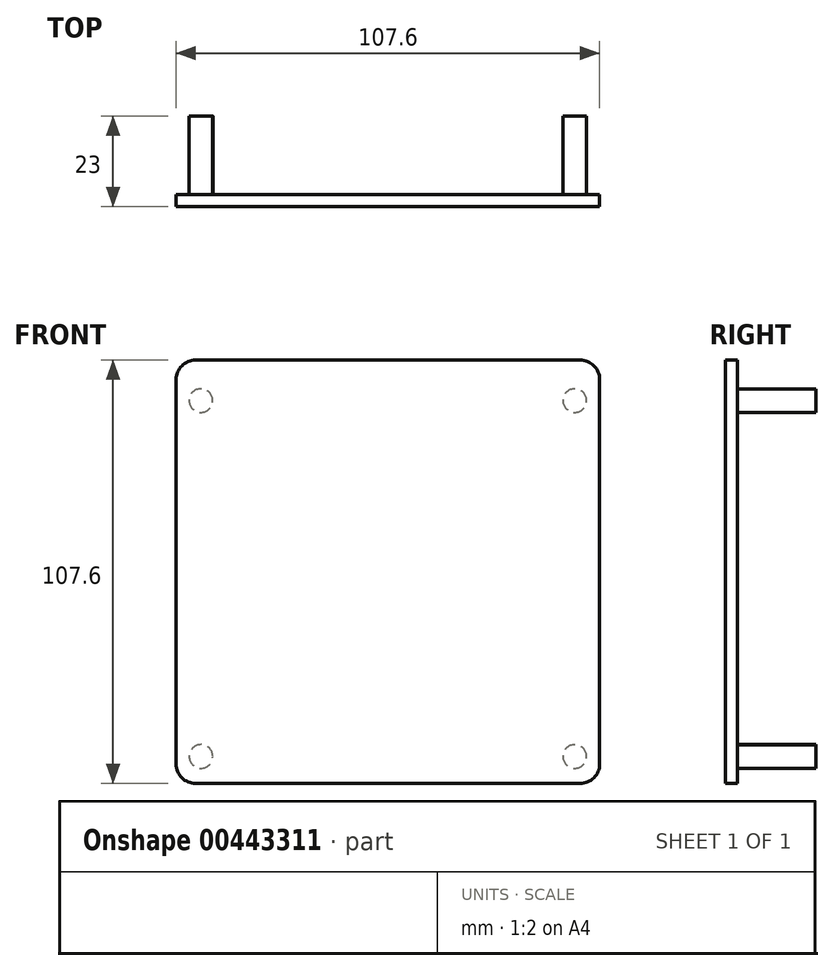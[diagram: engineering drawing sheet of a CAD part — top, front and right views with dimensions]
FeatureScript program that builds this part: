
annotation { "Feature Type Name" : "Feature", "Feature Type Description" : "" }
export const myFeature = defineFeature(function(context is Context, id is Id, definition is map)
    precondition{}
    {
        {
            var Q0;
            Q0=qCreatedBy(makeId("Front.planeOp"),FACE);
            var sketch = newSketch(context, id + "F0", { "sketchPlane" : qUnion([Q0])});
            skLineSegment(sketch, "E0.bottom", {"start": v(47.5, 45.2) * mm, "end": v(-47.5, 45.2) * mm});
            skLineSegment(sketch, "E0.top", {"start": v(47.5, -45.2) * mm, "end": v(-47.5, -45.2) * mm});
            skLineSegment(sketch, "E0.left", {"start": v(47.5, 45.2) * mm, "end": v(47.5, -45.2) * mm});
            skLineSegment(sketch, "E0.right", {"start": v(-47.5, 45.2) * mm, "end": v(-47.5, -45.2) * mm});
            skPoint(sketch, "E0.middle", {"position": v(0, 0) * mm});
            skLineSegment(sketch, "E1", {"start": v(-50.8, 50.5) * mm, "end": v(-50.8, -47.1) * mm});
            skLineSegment(sketch, "E2", {"start": v(-48.8, -49.1) * mm, "end": v(48.8, -49.1) * mm});
            skLineSegment(sketch, "E3", {"start": v(50.8, -47.1) * mm, "end": v(50.8, 50.5) * mm});
            skLineSegment(sketch, "E4", {"start": v(48.8, 52.5) * mm, "end": v(-48.8, 52.5) * mm});
            skPoint(sketch, "E5.visualSharp", {"position": v(50.8, 52.5) * mm});
            skPoint(sketch, "E6.visualSharp", {"position": v(50.8, -49.1) * mm});
            skArc(sketch, "E6.filletArc", {"start": v(48.8, -49.1) * mm, "mid": v(50.21, -48.51) * mm, "end": v(50.8, -47.1) * mm});
            skPoint(sketch, "E7.visualSharp", {"position": v(-50.8, -49.1) * mm});
            skArc(sketch, "E7.filletArc", {"start": v(-50.8, -47.1) * mm, "mid": v(-50.21, -48.51) * mm, "end": v(-48.8, -49.1) * mm});
            skArc(sketch, "E8.filletArc", {"start": v(50.8, 50.5) * mm, "mid": v(50.21, 51.91) * mm, "end": v(48.8, 52.5) * mm});
            skArc(sketch, "E9.filletArc", {"start": v(-48.8, 52.5) * mm, "mid": v(-50.21, 51.91) * mm, "end": v(-50.8, 50.5) * mm});
            skCircle(sketch, "E10", {"center": v(-47.5, 45.2) * mm, "radius": 1.5 * mm});
            skCircle(sketch, "E11", {"center": v(47.5, 45.2) * mm, "radius": 1.5 * mm});
            skCircle(sketch, "E12", {"center": v(47.5, -45.2) * mm, "radius": 1.5 * mm});
            skCircle(sketch, "E13", {"center": v(-47.5, -45.2) * mm, "radius": 1.5 * mm});
            skSolve(sketch);
        }
        {
            var Q0;
            Q0=qCreatedBy(makeId("Front.planeOp"),FACE);
            var sketch = newSketch(context, id + "F1", { "sketchPlane" : qUnion([Q0])});
            skArc(sketch, "E14.0", {"start": v(53.8, 50.5) * mm, "mid": v(52.34, 54.04) * mm, "end": v(48.8, 55.5) * mm});
            skLineSegment(sketch, "E14.1", {"start": v(53.8, -47.1) * mm, "end": v(53.8, 50.5) * mm});
            skLineSegment(sketch, "E14.2", {"start": v(48.8, 55.5) * mm, "end": v(-48.8, 55.5) * mm});
            skArc(sketch, "E14.3", {"start": v(48.8, -52.1) * mm, "mid": v(52.34, -50.64) * mm, "end": v(53.8, -47.1) * mm});
            skArc(sketch, "E14.4", {"start": v(-48.8, 55.5) * mm, "mid": v(-52.34, 54.04) * mm, "end": v(-53.8, 50.5) * mm});
            skLineSegment(sketch, "E14.5", {"start": v(-53.8, 50.5) * mm, "end": v(-53.8, -47.1) * mm});
            skArc(sketch, "E14.6", {"start": v(-53.8, -47.1) * mm, "mid": v(-52.34, -50.64) * mm, "end": v(-48.8, -52.1) * mm});
            skLineSegment(sketch, "E14.7", {"start": v(-48.8, -52.1) * mm, "end": v(48.8, -52.1) * mm});
            skSolve(sketch);
        }
        {
            var Q0;
            Q0=qCreatedBy(makeId("Front.planeOp"),FACE);
            var sketch = newSketch(context, id + "F2", { "sketchPlane" : qUnion([Q0])});
            skCircle(sketch, "E15", {"center": v(-47.5, 45.2) * mm, "radius": 3 * mm});
            skCircle(sketch, "E16", {"center": v(47.48, 45.19) * mm, "radius": 3 * mm});
            skCircle(sketch, "E17", {"center": v(47.47, -45.23) * mm, "radius": 3 * mm});
            skCircle(sketch, "E18", {"center": v(-47.47, -45.22) * mm, "radius": 3 * mm});
            skSolve(sketch);
        }
        {
            var Q0;
            Q0 = qSketchRegion(id + "F2", true);
            extrude(context, id + "F3", {"entities" : qUnion([Q0]), "oppositeDirection" : true, "depth" : 20 * mm});
        }
        {
            var Q0;
            Q0=makeQuery(id+"F1.imprint","IMPRINT",FACE,{"disambiguationData":[TD([[makeQuery(id+"F1.imprint","IMPRINT",EDGE,{"derivedFrom":sQuery(id+"F1.wireOp",EDGE,"E14.0")}),1.0]])]});
            extrude(context, id + "F4", {"entities" : qUnion([Q0]), "depth" : 3 * mm});
        }
    });
